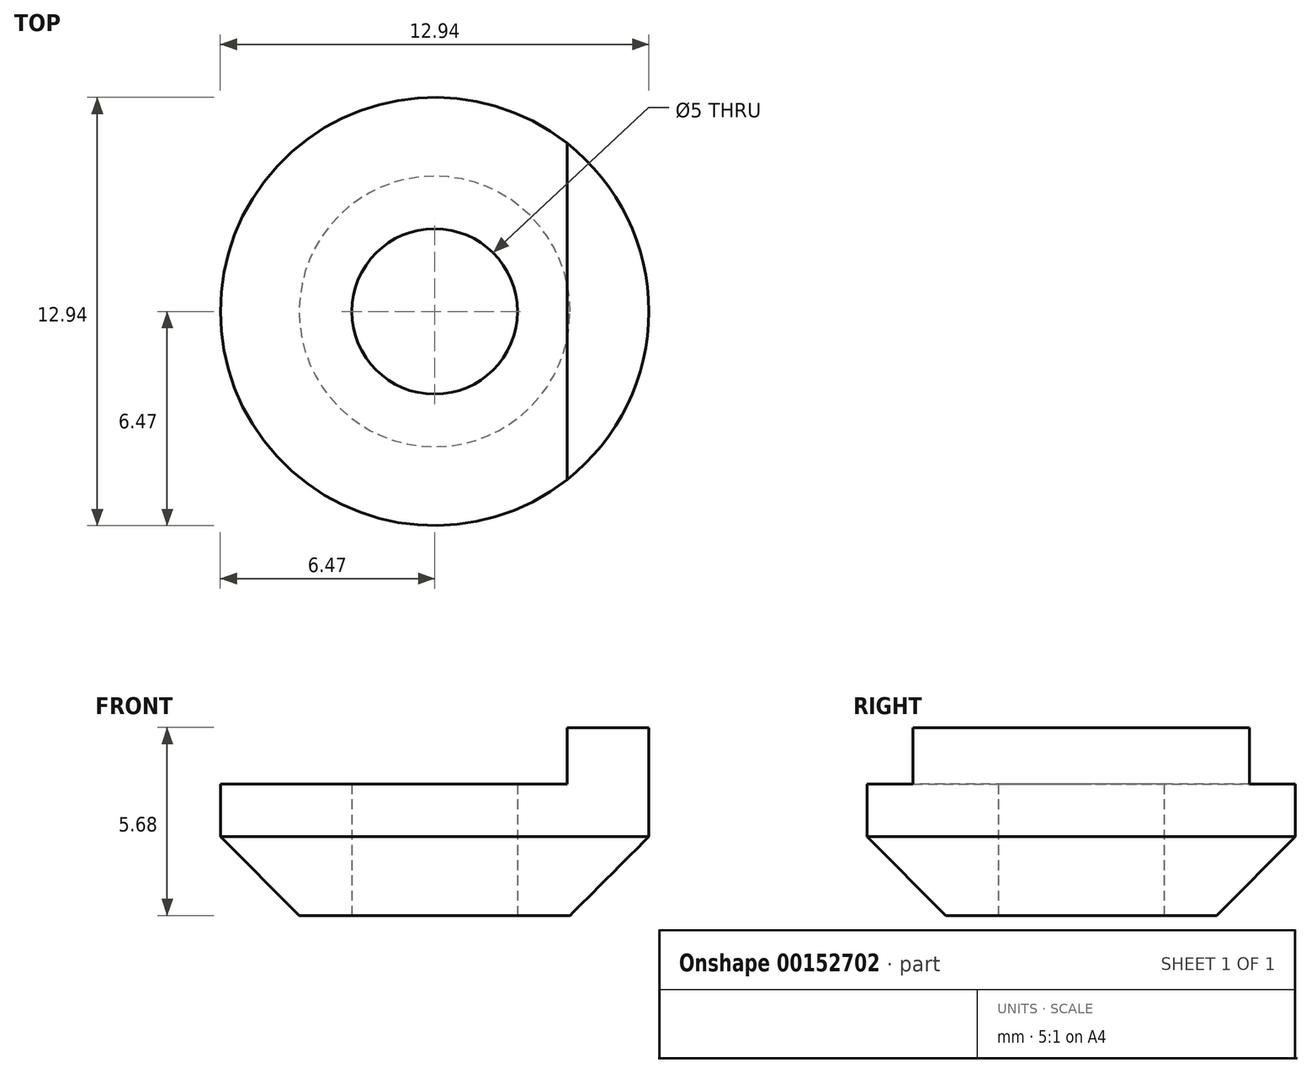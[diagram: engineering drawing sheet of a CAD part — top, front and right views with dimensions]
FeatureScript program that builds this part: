
annotation { "Feature Type Name" : "Feature", "Feature Type Description" : "" }
export const myFeature = defineFeature(function(context is Context, id is Id, definition is map)
    precondition{}
    {
        {
            var Q0;
            Q0=qCreatedBy(makeId("Top.planeOp"),FACE);
            var sketch = newSketch(context, id + "F0", { "sketchPlane" : qUnion([Q0])});
            skCircle(sketch, "E0", {"center": v(0, 0) * mm, "radius": 2.5 * mm});
            skCircle(sketch, "E1", {"center": v(0, 0) * mm, "radius": 6.47 * mm});
            skSolve(sketch);
        }
        {
            var Q0;
            Q0 = qSketchRegion(id + "F0", true);
            extrude(context, id + "F1", {"entities" : qUnion([Q0]), "depth" : 5.68 * mm});
        }
        {
            var Q0;
            Q0=makeQuery(id+"F1.opExtrude","CAP_EDGE",EDGE,{"disambiguationData":[OSD([sQuery(id+"F0.wireOp",EDGE,"E1")])],"isStart":true});
            chamfer(context, id + "F2", {"entities" : qUnion([Q0]), "width" : 2.38 * mm, "tangentPropagation" : true});
        }
        {
            var Q0;
            Q0=makeQuery(id+"F1.opExtrude","CAP_FACE",FACE,{"disambiguationData":[OSD([sQuery(id+"F0.wireOp",EDGE,"E0"),sQuery(id+"F0.wireOp",EDGE,"E1")])],"isStart":false});
            var sketch = newSketch(context, id + "F3", { "sketchPlane" : qUnion([Q0])});
            skLineSegment(sketch, "E2", {"start": v(0, 0) * mm, "end": v(4, 0) * mm, "construction": true});
            skLineSegment(sketch, "E3.bottom", {"start": v(4, -6.47) * mm, "end": v(-6.47, -6.47) * mm});
            skLineSegment(sketch, "E3.top", {"start": v(4, 6.47) * mm, "end": v(-6.47, 6.47) * mm});
            skLineSegment(sketch, "E3.left", {"start": v(4, -6.47) * mm, "end": v(4, 6.47) * mm});
            skLineSegment(sketch, "E3.right", {"start": v(-6.47, -6.47) * mm, "end": v(-6.47, 6.47) * mm});
            skSolve(sketch);
        }
        {
            var Q0;
            Q0 = qSketchRegion(id + "F3", true);
            extrude(context, id + "F4", {"entities" : qUnion([Q0]), "operationType" : NewBodyOperationType.REMOVE, "oppositeDirection" : true, "depth" : 1.7 * mm});
        }
    });
